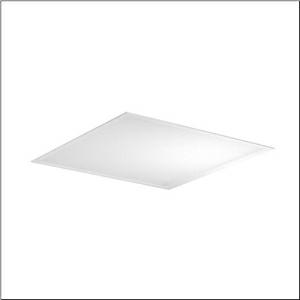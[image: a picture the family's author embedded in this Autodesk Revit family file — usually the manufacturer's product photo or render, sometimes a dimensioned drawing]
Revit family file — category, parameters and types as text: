
# Revit family: apollon_21_square_51mq12w72414
name_source: partatom
category: Lighting Fixtures
units: mm (PartAtom-declared; Revit-internal decimal feet)

## family parameters
Cut with Voids When Loaded = No
Host = Face
Light Source = No
Part Type = Normal
Room Calculation Point = No
Round Connector Dimension = Use Diameter
Shared = No

## types (1)
- Apollon 21 square (1 x LED, 4200 lm, 23.3 W, 4000K)
    Apparent Load = 23 VA
    CIE Flux Codes = 60 87 97 100 100
    Color Rendering = 80
    Color Temperature = 4000K
    Default Elevation = 1800 mm
    Description = Apollon 21 square, office luminaire, primary optical cover: micro prismatic cover, of PMMA, CAT 2 (L<= 3000cd/m²), light emission: direct distribution, primary light characteristic: symmetric, installation type: lay-in mounting, recessed, LED, rated luminous flux: 4.200lm, luminous efficacy: 180lm/W, light colour: 840, colour temperature: 4000K, control gear: ON/OFF, with terminal, 3-pole, mains connection: 220..240V, AC/DC, 0/50..60Hz, rated input power: 23W, suitable for self-contained emergency lighting element 59MQE002602A with integrated self-test function according to EN 60598-2-22, housing, of aluminium, coated, traffic white (RAL 9016), module: M600, length: 595mm, width: 595mm, height: 55mm, housing upper side, of sheet steel, galvanised, protection rating (complete): IP20, protection rating (lamp compartment, on room side): IP50, insulation class (complete): insulation class II (safety insulation), certification: CE, ENEC, impact resistance: IK03, permissible operating ambient temperature: -20..+45°C, standard: EN 60598-2-22, corresponds to IFS (International Featured Standards) requirements for safety and quality in the food industry, packaging unit: 1 piece
    Height = 0 mm  [stored 0 ft]
    Lamp = 1 x LED
    Lamp Light Flux = 4200 lm
    Lamp Power = 23.3 W
    Lamp count = 1
    Length = 595 mm
    Luminous efficacy = 180 lm/W
    Manufacturer = Siteco
    ModVariant = No
    Model = 51MQ12W72414
    Mounting Place = Ceiling
    Mounting Type = Recessed
    Number of Poles = 1
    OnlyDefault = Yes
    Power Factor = 1
    Product Name = Apollon 21 square
    Product group = office luminaire | ceiling recessed
    ProductGroupID = 400
    Protection Class = Protection class II
    Protection Degree = IP 20
    RLX_Detail_Level = 1
    RLX_Emergency_Light_Flux = 0 lm
    RLX_Emergency_Type = 0
    RLX_Emergency_Type_DB = No
    RlxData = <blob elided: 97193 chars, md5=8a1a5b3a>
    Socket = socket
    Standby Power = 0 W
    System Light Flux = 4200 lm
    System Power = 23 W
    Type Comments = Product without accessories
    Type Image = l_1291049.jpg
    URL = http://relux.com
    VarID = ---
    Voltage = 0 V
    Weight = 0.00 kg
    Width = 595 mm

note: [stored X ft] marks values corroborated as IEEE doubles in the binary element streams (Revit-internal decimal feet)

## geometry (parser evidence)
native form markers: Blend x4, Sweep x9
no freeform markers — native parametric forms only
